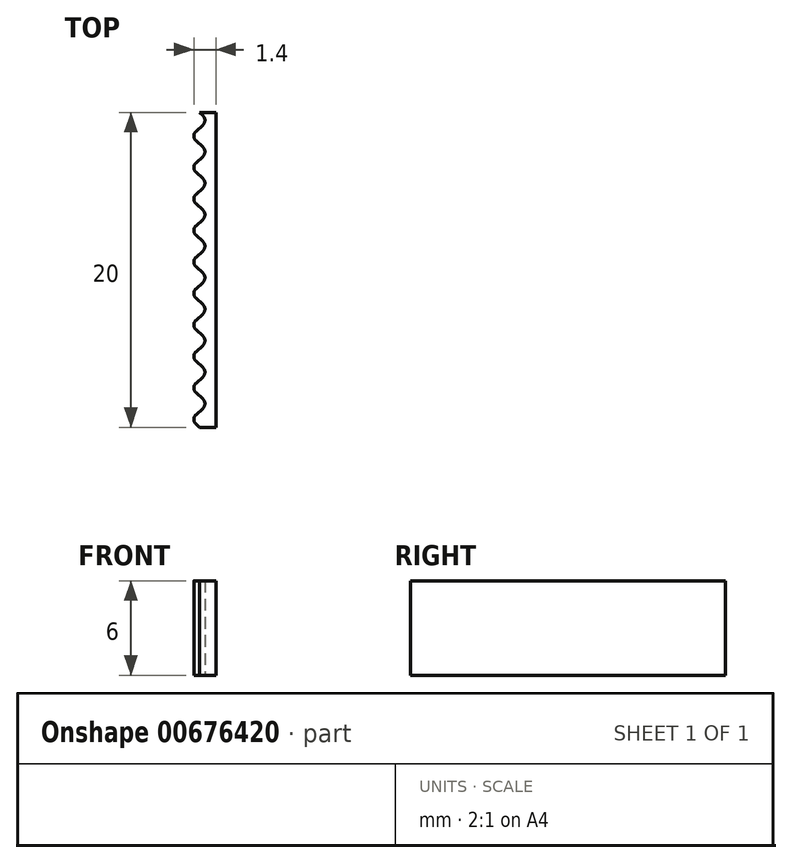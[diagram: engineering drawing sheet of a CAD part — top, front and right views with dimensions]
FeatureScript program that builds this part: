
annotation { "Feature Type Name" : "Feature", "Feature Type Description" : "" }
export const myFeature = defineFeature(function(context is Context, id is Id, definition is map)
    precondition{}
    {
        {
            var Q0;
            Q0=qCreatedBy(makeId("Top.planeOp"),FACE);
            var sketch = newSketch(context, id + "F0", { "sketchPlane" : qUnion([Q0])});
            skLineSegment(sketch, "E0.bottom", {"start": v(0, 10) * mm, "end": v(0.7, 10) * mm});
            skLineSegment(sketch, "E0.top", {"start": v(0, -10) * mm, "end": v(0.7, -10) * mm});
            skLineSegment(sketch, "E0.left", {"start": v(0, 10) * mm, "end": v(0, -10) * mm, "construction": true});
            skLineSegment(sketch, "E0.right", {"start": v(0.7, 10) * mm, "end": v(0.7, -10) * mm});
            skLineSegment(sketch, "E1", {"start": v(-0.35, 10) * mm, "end": v(-0.35, -10) * mm, "construction": true});
            skLineSegment(sketch, "E2", {"start": v(-0.7, 10) * mm, "end": v(-0.7, -10) * mm, "construction": true});
            skLineSegment(sketch, "E3", {"start": v(-0.7, 10) * mm, "end": v(0, 10) * mm, "construction": true});
            skLineSegment(sketch, "E4", {"start": v(-0.7, -10) * mm, "end": v(0, -10) * mm, "construction": true});
            skLineSegment(sketch, "E5", {"start": v(-0.35, -10) * mm, "end": v(0, -10) * mm});
            skLineSegment(sketch, "E6", {"start": v(-0.35, 10) * mm, "end": v(0, 10) * mm});
            skArc(sketch, "E7", {"start": v(-0.57, -9.2) * mm, "mid": v(-0.7, -9.5) * mm, "end": v(-0.57, -9.8) * mm});
            skArc(sketch, "E8", {"start": v(-0.13, -8.8) * mm, "mid": v(0, -8.5) * mm, "end": v(-0.13, -8.2) * mm});
            skLineSegment(sketch, "E9", {"start": v(-0.35, -8) * mm, "end": v(-0.13, -8.2) * mm});
            skLineSegment(sketch, "E10", {"start": v(-0.57, -9.2) * mm, "end": v(-0.13, -8.8) * mm});
            skLineSegment(sketch, "E11", {"start": v(-0.57, -9.8) * mm, "end": v(-0.35, -10) * mm});
            skLineSegment(sketch, "E12.0.1.0", {"start": v(-0.57, -7.8) * mm, "end": v(-0.35, -8) * mm});
            skArc(sketch, "E12.0.1.1", {"start": v(-0.57, -7.2) * mm, "mid": v(-0.7, -7.5) * mm, "end": v(-0.57, -7.8) * mm});
            skLineSegment(sketch, "E12.0.1.2", {"start": v(-0.57, -7.2) * mm, "end": v(-0.13, -6.8) * mm});
            skArc(sketch, "E12.0.1.3", {"start": v(-0.13, -6.8) * mm, "mid": v(0, -6.5) * mm, "end": v(-0.13, -6.2) * mm});
            skLineSegment(sketch, "E12.0.1.4", {"start": v(-0.35, -6) * mm, "end": v(-0.13, -6.2) * mm});
            skLineSegment(sketch, "E12.0.2.0", {"start": v(-0.57, -5.8) * mm, "end": v(-0.35, -6) * mm});
            skArc(sketch, "E12.0.2.1", {"start": v(-0.57, -5.2) * mm, "mid": v(-0.7, -5.5) * mm, "end": v(-0.57, -5.8) * mm});
            skLineSegment(sketch, "E12.0.2.2", {"start": v(-0.57, -5.2) * mm, "end": v(-0.13, -4.8) * mm});
            skArc(sketch, "E12.0.2.3", {"start": v(-0.13, -4.8) * mm, "mid": v(0, -4.5) * mm, "end": v(-0.13, -4.2) * mm});
            skLineSegment(sketch, "E12.0.2.4", {"start": v(-0.35, -4) * mm, "end": v(-0.13, -4.2) * mm});
            skLineSegment(sketch, "E12.0.3.0", {"start": v(-0.57, -3.8) * mm, "end": v(-0.35, -4) * mm});
            skArc(sketch, "E12.0.3.1", {"start": v(-0.57, -3.2) * mm, "mid": v(-0.7, -3.5) * mm, "end": v(-0.57, -3.8) * mm});
            skLineSegment(sketch, "E12.0.3.2", {"start": v(-0.57, -3.2) * mm, "end": v(-0.13, -2.8) * mm});
            skArc(sketch, "E12.0.3.3", {"start": v(-0.13, -2.8) * mm, "mid": v(0, -2.5) * mm, "end": v(-0.13, -2.2) * mm});
            skLineSegment(sketch, "E12.0.3.4", {"start": v(-0.35, -2) * mm, "end": v(-0.13, -2.2) * mm});
            skLineSegment(sketch, "E12.0.4.0", {"start": v(-0.57, -1.8) * mm, "end": v(-0.35, -2) * mm});
            skArc(sketch, "E12.0.4.1", {"start": v(-0.57, -1.2) * mm, "mid": v(-0.7, -1.5) * mm, "end": v(-0.57, -1.8) * mm});
            skLineSegment(sketch, "E12.0.4.2", {"start": v(-0.57, -1.2) * mm, "end": v(-0.13, -0.8) * mm});
            skArc(sketch, "E12.0.4.3", {"start": v(-0.13, -0.8) * mm, "mid": v(0, -0.5) * mm, "end": v(-0.13, -0.2) * mm});
            skLineSegment(sketch, "E12.0.4.4", {"start": v(-0.35, 0) * mm, "end": v(-0.13, -0.2) * mm});
            skLineSegment(sketch, "E12.0.5.0", {"start": v(-0.57, 0.2) * mm, "end": v(-0.35, 0) * mm});
            skArc(sketch, "E12.0.5.1", {"start": v(-0.57, 0.8) * mm, "mid": v(-0.7, 0.5) * mm, "end": v(-0.57, 0.2) * mm});
            skLineSegment(sketch, "E12.0.5.2", {"start": v(-0.57, 0.8) * mm, "end": v(-0.13, 1.2) * mm});
            skArc(sketch, "E12.0.5.3", {"start": v(-0.13, 1.2) * mm, "mid": v(0, 1.5) * mm, "end": v(-0.13, 1.8) * mm});
            skLineSegment(sketch, "E12.0.5.4", {"start": v(-0.35, 2) * mm, "end": v(-0.13, 1.8) * mm});
            skLineSegment(sketch, "E12.0.6.0", {"start": v(-0.57, 2.2) * mm, "end": v(-0.35, 2) * mm});
            skArc(sketch, "E12.0.6.1", {"start": v(-0.57, 2.8) * mm, "mid": v(-0.7, 2.5) * mm, "end": v(-0.57, 2.2) * mm});
            skLineSegment(sketch, "E12.0.6.2", {"start": v(-0.57, 2.8) * mm, "end": v(-0.13, 3.2) * mm});
            skArc(sketch, "E12.0.6.3", {"start": v(-0.13, 3.2) * mm, "mid": v(0, 3.5) * mm, "end": v(-0.13, 3.8) * mm});
            skLineSegment(sketch, "E12.0.6.4", {"start": v(-0.35, 4) * mm, "end": v(-0.13, 3.8) * mm});
            skLineSegment(sketch, "E12.0.7.0", {"start": v(-0.57, 4.2) * mm, "end": v(-0.35, 4) * mm});
            skArc(sketch, "E12.0.7.1", {"start": v(-0.57, 4.8) * mm, "mid": v(-0.7, 4.5) * mm, "end": v(-0.57, 4.2) * mm});
            skLineSegment(sketch, "E12.0.7.2", {"start": v(-0.57, 4.8) * mm, "end": v(-0.13, 5.2) * mm});
            skArc(sketch, "E12.0.7.3", {"start": v(-0.13, 5.2) * mm, "mid": v(0, 5.5) * mm, "end": v(-0.13, 5.8) * mm});
            skLineSegment(sketch, "E12.0.7.4", {"start": v(-0.35, 6) * mm, "end": v(-0.13, 5.8) * mm});
            skLineSegment(sketch, "E12.0.8.0", {"start": v(-0.57, 6.2) * mm, "end": v(-0.35, 6) * mm});
            skArc(sketch, "E12.0.8.1", {"start": v(-0.57, 6.8) * mm, "mid": v(-0.7, 6.5) * mm, "end": v(-0.57, 6.2) * mm});
            skLineSegment(sketch, "E12.0.8.2", {"start": v(-0.57, 6.8) * mm, "end": v(-0.13, 7.2) * mm});
            skArc(sketch, "E12.0.8.3", {"start": v(-0.13, 7.2) * mm, "mid": v(0, 7.5) * mm, "end": v(-0.13, 7.8) * mm});
            skLineSegment(sketch, "E12.0.8.4", {"start": v(-0.35, 8) * mm, "end": v(-0.13, 7.8) * mm});
            skLineSegment(sketch, "E12.0.9.0", {"start": v(-0.57, 8.2) * mm, "end": v(-0.35, 8) * mm});
            skArc(sketch, "E12.0.9.1", {"start": v(-0.57, 8.8) * mm, "mid": v(-0.7, 8.5) * mm, "end": v(-0.57, 8.2) * mm});
            skLineSegment(sketch, "E12.0.9.2", {"start": v(-0.57, 8.8) * mm, "end": v(-0.13, 9.2) * mm});
            skArc(sketch, "E12.0.9.3", {"start": v(-0.13, 9.2) * mm, "mid": v(0, 9.5) * mm, "end": v(-0.13, 9.8) * mm});
            skLineSegment(sketch, "E12.0.9.4", {"start": v(-0.35, 10) * mm, "end": v(-0.13, 9.8) * mm});
            skLineSegment(sketch, "E12.direction1", {"start": v(-0.57, -9.8) * mm, "end": v(1.72, -10.89) * mm, "construction": true});
            skLineSegment(sketch, "E12.direction2", {"start": v(-0.57, -9.8) * mm, "end": v(-0.57, -7.8) * mm, "construction": true});
            skSolve(sketch);
        }
        {
            var Q0;
            Q0=makeQuery(id+"F0.imprint","IMPRINT",FACE,{"disambiguationData":[TD([[makeQuery(id+"F0.imprint","IMPRINT",EDGE,{"derivedFrom":sQuery(id+"F0.wireOp",EDGE,"E0.bottom")}),-1.0]])]});
            extrude(context, id + "F1", {"entities" : qUnion([Q0]), "flatOperationType" : FlatOperationType.REMOVE, "depth" : 6 * mm, "offsetDistance" : 25 * mm, "domain" : OperationDomain.MODEL, "symmetric" : true});
        }
    });
